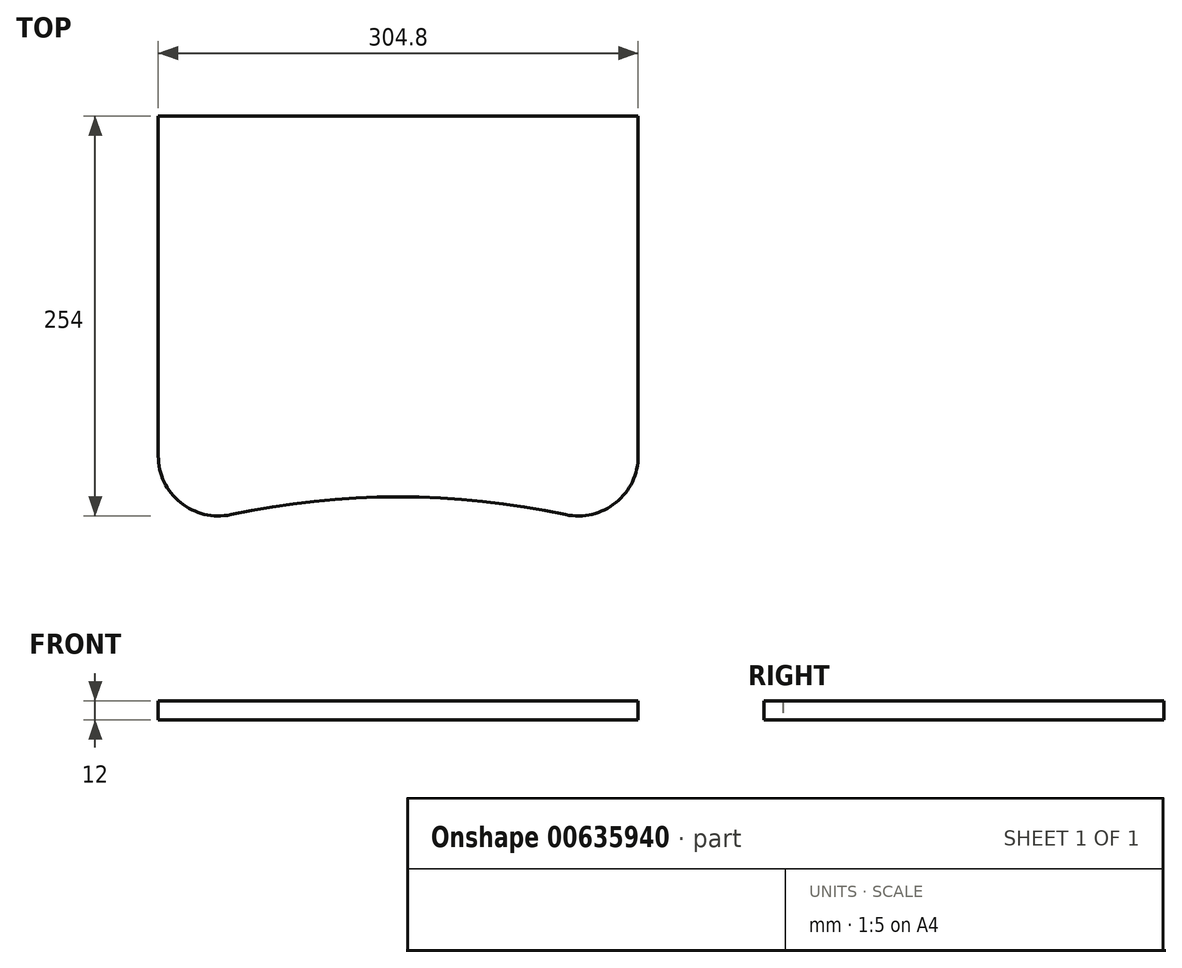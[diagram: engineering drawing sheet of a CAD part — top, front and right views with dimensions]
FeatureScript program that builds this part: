
annotation { "Feature Type Name" : "Feature", "Feature Type Description" : "" }
export const myFeature = defineFeature(function(context is Context, id is Id, definition is map)
    precondition{}
    {
        {
            var Q0;
            Q0=qCreatedBy(makeId("Top.planeOp"),FACE);
            var sketch = newSketch(context, id + "F0", { "sketchPlane" : qUnion([Q0])});
            skLineSegment(sketch, "E0.bottom", {"start": v(-152.4, 127) * mm, "end": v(152.4, 127) * mm});
            skLineSegment(sketch, "E0.top", {"start": v(-152.4, -127) * mm, "end": v(152.4, -127) * mm, "construction": true});
            skLineSegment(sketch, "E0.left", {"start": v(-152.4, 127) * mm, "end": v(-152.4, -88.9) * mm});
            skLineSegment(sketch, "E0.right", {"start": v(152.4, 127) * mm, "end": v(152.4, -88.9) * mm});
            skPoint(sketch, "E0.middle", {"position": v(0, 0) * mm});
            skArc(sketch, "E1", {"start": v(106.33, -126.16) * mm, "mid": v(0, -114.9) * mm, "end": v(-106.33, -126.16) * mm});
            skArc(sketch, "E2", {"start": v(106.33, -126.16) * mm, "mid": v(138.26, -118.53) * mm, "end": v(152.4, -88.9) * mm});
            skArc(sketch, "E3", {"start": v(-106.33, -126.16) * mm, "mid": v(-138.26, -118.53) * mm, "end": v(-152.4, -88.9) * mm});
            skLineSegment(sketch, "E4", {"start": v(0, 690.93) * mm, "end": v(0, -666.3) * mm, "construction": true});
            skLineSegment(sketch, "E5", {"start": v(152.4, -88.9) * mm, "end": v(152.4, -127) * mm, "construction": true});
            skLineSegment(sketch, "E6", {"start": v(-152.4, -88.9) * mm, "end": v(-152.4, -127) * mm, "construction": true});
            skSolve(sketch);
        }
        {
            var Q0;
            Q0 = qSketchRegion(id + "F0", true);
            extrude(context, id + "F1", {"entities" : qUnion([Q0]), "depth" : 12 * mm, "offsetDistance" : 25.4 * mm});
        }
    });
